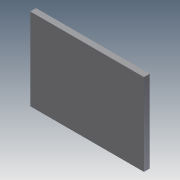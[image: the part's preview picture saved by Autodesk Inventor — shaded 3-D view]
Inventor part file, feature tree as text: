
AUTODESK INVENTOR PART (.ipt)
format: ipt  version: 2011 (Build 150239000, 239)  size: 75,264 bytes
history: native  units: in
note: dims shown in document units (in); Inventor stores cm internally (conversion verified against a paired STEP export)
features: extrude x2, sketch x2
ambient origin geometry x8: Origin, YZ Plane, XZ Plane, XY Plane, X Axis, Y Axis, Z Axis, Center Point
bodies: Solid1 (feature_tree)
feature tree (4):
  extrude  "Extrusion1"  Depth=1.7717in
  extrude  "Extrusion2"  Depth=0.25in TaperAngle=0.0deg
  sketch  "Sketch1"  dims[d0=2.2047in d1=1.7717in]
  sketch  "Sketch2"  dims[d2=0.125in d3=0.0in d4=0.25in d5=0.0in]
